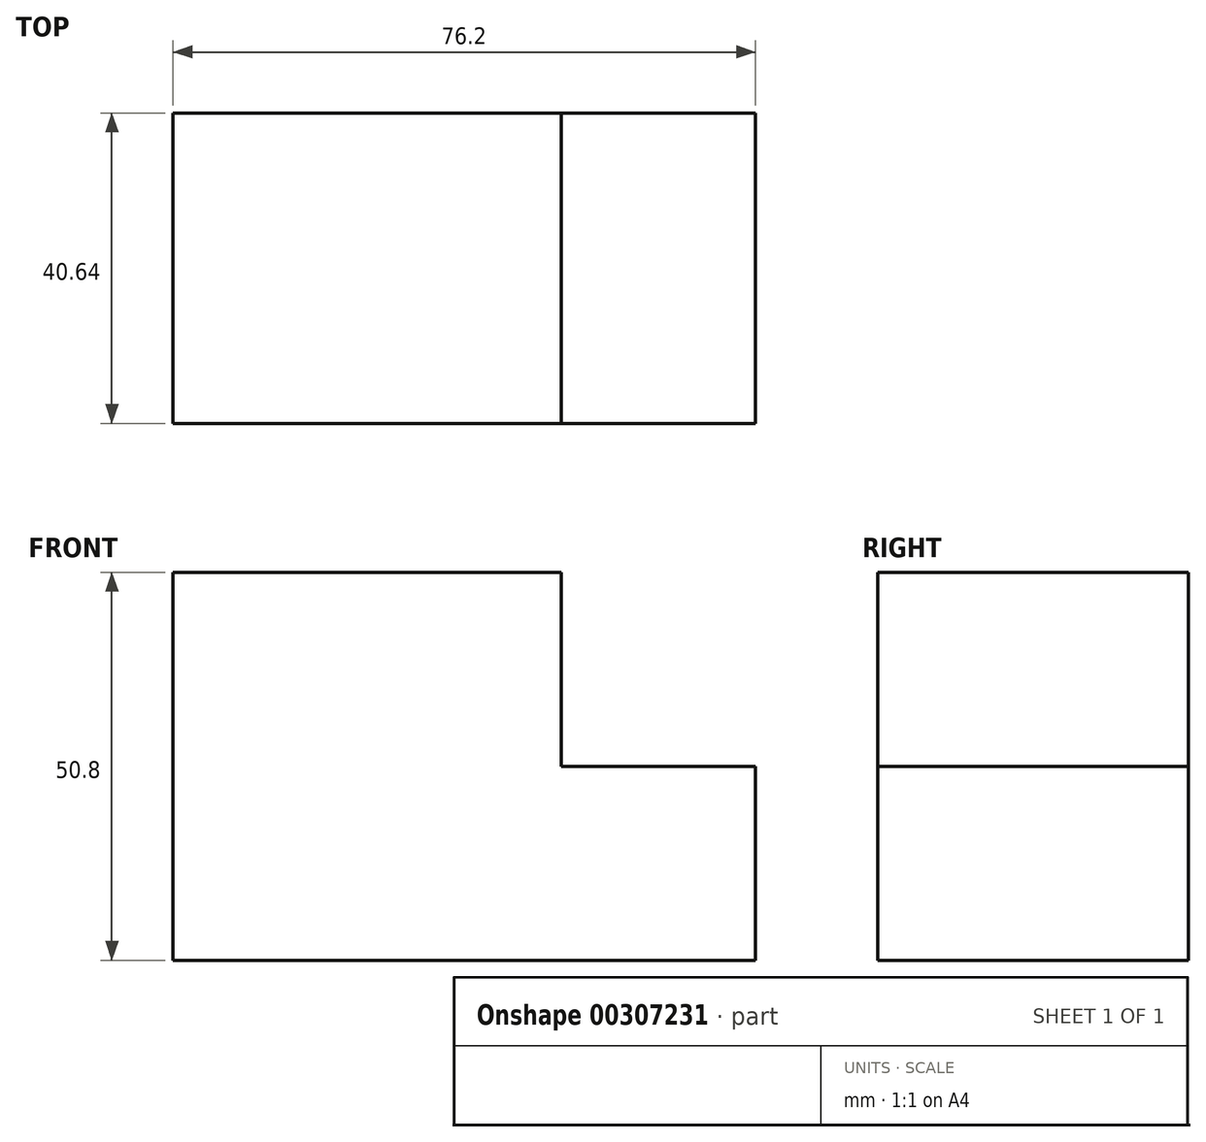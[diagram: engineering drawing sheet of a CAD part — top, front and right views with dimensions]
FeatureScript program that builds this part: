
annotation { "Feature Type Name" : "Feature", "Feature Type Description" : "" }
export const myFeature = defineFeature(function(context is Context, id is Id, definition is map)
    precondition{}
    {
        {
            var Q0;
            Q0=qCreatedBy(makeId("Front.planeOp"),FACE);
            var sketch = newSketch(context, id + "F0", { "sketchPlane" : qUnion([Q0])});
            skLineSegment(sketch, "E0", {"start": v(-49.5, -32.78) * mm, "end": v(26.7, -32.78) * mm});
            skLineSegment(sketch, "E1", {"start": v(26.7, -32.78) * mm, "end": v(26.7, -7.38) * mm});
            skLineSegment(sketch, "E2", {"start": v(26.7, -7.38) * mm, "end": v(1.3, -7.38) * mm});
            skLineSegment(sketch, "E3", {"start": v(1.3, -7.38) * mm, "end": v(1.3, 18.02) * mm});
            skLineSegment(sketch, "E4", {"start": v(1.3, 18.02) * mm, "end": v(-49.5, 18.02) * mm});
            skLineSegment(sketch, "E5", {"start": v(-49.5, 18.02) * mm, "end": v(-49.5, -32.78) * mm});
            skSolve(sketch);
        }
        {
            var Q0;
            Q0=makeQuery(id+"F0.imprint","IMPRINT",FACE,{"disambiguationData":[TD([[makeQuery(id+"F0.imprint","IMPRINT",EDGE,{"derivedFrom":sQuery(id+"F0.wireOp",EDGE,"E0")}),1.0]])]});
            extrude(context, id + "F1", {"entities" : qUnion([Q0]), "depth" : 40.64 * mm});
        }
    });
